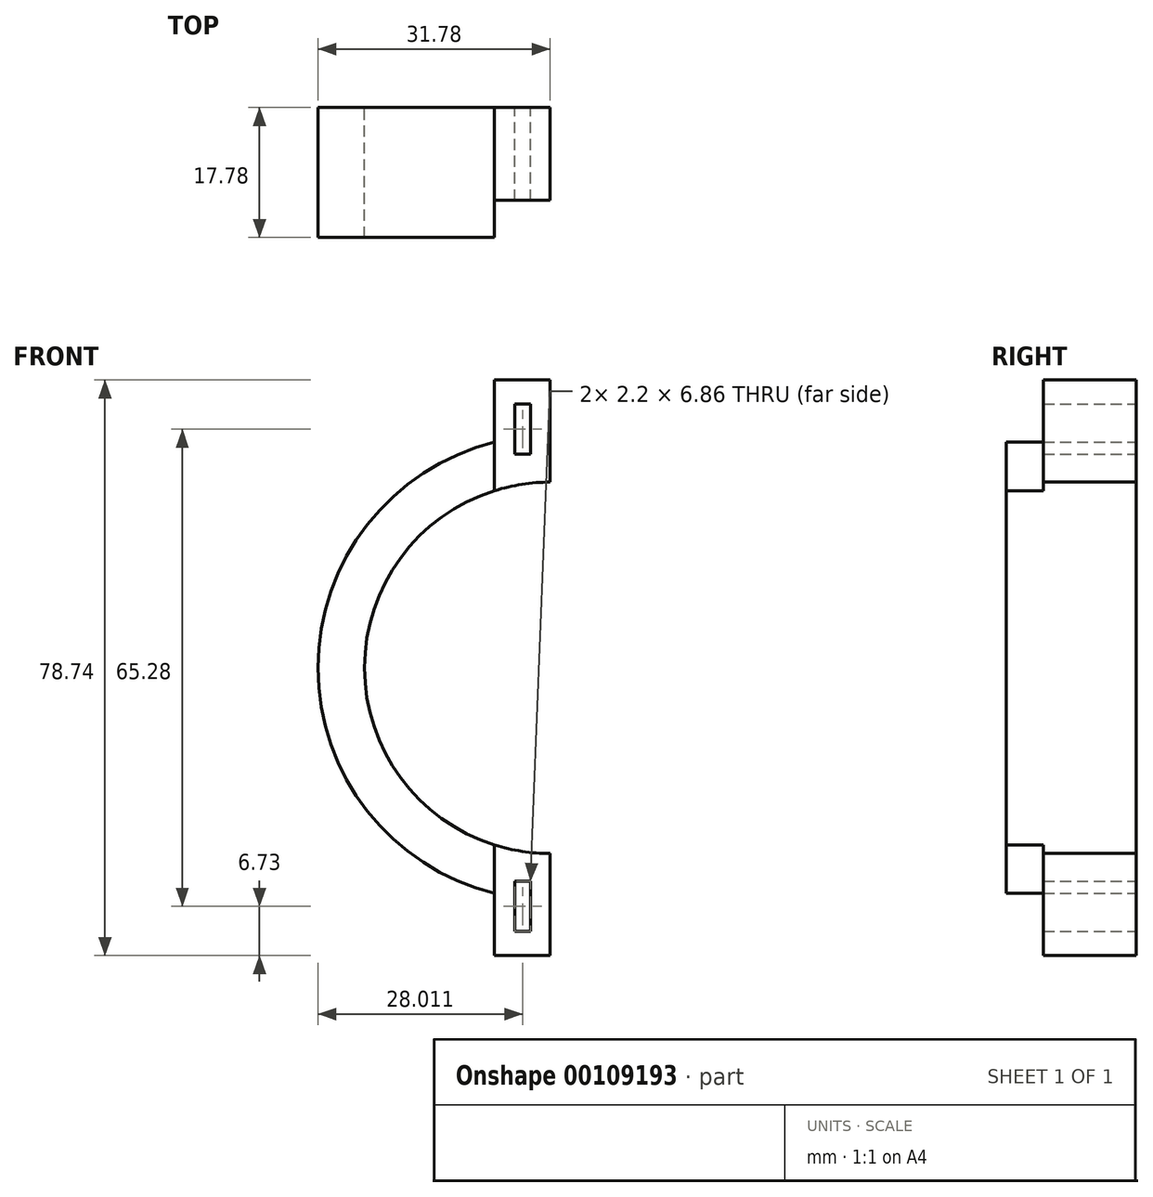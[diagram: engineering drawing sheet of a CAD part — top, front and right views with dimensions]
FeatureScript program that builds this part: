
annotation { "Feature Type Name" : "Feature", "Feature Type Description" : "" }
export const myFeature = defineFeature(function(context is Context, id is Id, definition is map)
    precondition{}
    {
        {
            var Q0;
            Q0=qCreatedBy(makeId("Front.planeOp"),FACE);
            var sketch = newSketch(context, id + "F0", { "sketchPlane" : qUnion([Q0])});
            skLineSegment(sketch, "E0", {"start": v(0, 42.41) * mm, "end": v(0, -42.81) * mm, "construction": true});
            skArc(sketch, "E1", {"start": v(0, 25.4) * mm, "mid": v(-25.4, 0) * mm, "end": v(0, -25.4) * mm});
            skArc(sketch, "E2", {"start": v(0, 31.78) * mm, "mid": v(-31.78, 0) * mm, "end": v(0, -31.78) * mm});
            skLineSegment(sketch, "E3.top", {"start": v(0, 39.37) * mm, "end": v(-7.62, 39.37) * mm});
            skLineSegment(sketch, "E3.left", {"start": v(0, 25.4) * mm, "end": v(0, 39.37) * mm});
            skLineSegment(sketch, "E3.right", {"start": v(-7.62, 24.23) * mm, "end": v(-7.62, 39.37) * mm});
            skLineSegment(sketch, "E4.MirrorCS", {"start": v(0, -39.37) * mm, "end": v(-7.62, -39.37) * mm});
            skLineSegment(sketch, "E5.MirrorCS", {"start": v(-7.62, -24.23) * mm, "end": v(-7.62, -39.37) * mm});
            skLineSegment(sketch, "E6.MirrorCS", {"start": v(0, -25.4) * mm, "end": v(0, -39.37) * mm});
            skLineSegment(sketch, "E7.bottom", {"start": v(-4.87, 36.07) * mm, "end": v(-2.67, 36.07) * mm});
            skLineSegment(sketch, "E7.top", {"start": v(-4.87, 29.21) * mm, "end": v(-2.67, 29.21) * mm});
            skLineSegment(sketch, "E7.left", {"start": v(-4.87, 36.07) * mm, "end": v(-4.87, 29.21) * mm});
            skLineSegment(sketch, "E7.right", {"start": v(-2.67, 36.07) * mm, "end": v(-2.67, 29.21) * mm});
            skLineSegment(sketch, "E8.MirrorCS", {"start": v(-4.87, -36.07) * mm, "end": v(-2.67, -36.07) * mm});
            skLineSegment(sketch, "E9.MirrorCS", {"start": v(-4.87, -36.07) * mm, "end": v(-4.87, -29.21) * mm});
            skLineSegment(sketch, "E10.MirrorCS", {"start": v(-2.67, -36.07) * mm, "end": v(-2.67, -29.21) * mm});
            skLineSegment(sketch, "E11.MirrorCS", {"start": v(-4.87, -29.21) * mm, "end": v(-2.67, -29.21) * mm});
            skPoint(sketch, "E12.middle.positionSnap0", {"position": v(-31.78, 0) * mm});
            skPoint(sketch, "E12.centerSnap0", {"position": v(-31.78, 0) * mm});
            skSolve(sketch);
        }
        {
            var Q0;
            Q0=qSketchRegion(id+"F0",true);
            var Q1;
            {var subQ0=sQuery(id+"F0.wireOp",EDGE,"E3.right");var subQ1=sQuery(id+"F0.wireOp",EDGE,"E1");var subQ2=makeQuery(id+"F0.imprint","INTERSECT",VERTEX,{"derivedFrom":[subQ1,subQ0]});Q1=makeQuery(id+"F0.imprint","IMPRINT",FACE,{"disambiguationData":[TD([[makeQuery(id+"F0.imprint","IMPRINT",EDGE,{"disambiguationData":[TD([[subQ2,-1.0]])],"derivedFrom":subQ1}),-1.0]])]});}
            extrude(context, id + "F1", {"entities" : qUnion([Q0, Q1]), "depth" : 12.7 * mm});
        }
        {
            var Q0;
            {var subQ0=sQuery(id+"F0.wireOp",EDGE,"E3.right");var subQ1=sQuery(id+"F0.wireOp",EDGE,"E1");var subQ2=makeQuery(id+"F0.imprint","INTERSECT",VERTEX,{"derivedFrom":[subQ1,subQ0]});Q0=makeQuery(id+"F0.imprint","IMPRINT",FACE,{"disambiguationData":[TD([[makeQuery(id+"F0.imprint","IMPRINT",EDGE,{"disambiguationData":[TD([[subQ2,-1.0]])],"derivedFrom":subQ1}),-1.0]])]});}
            extrude(context, id + "F2", {"entities" : qUnion([Q0]), "operationType" : NewBodyOperationType.ADD, "depth" : 17.78 * mm});
        }
    });
